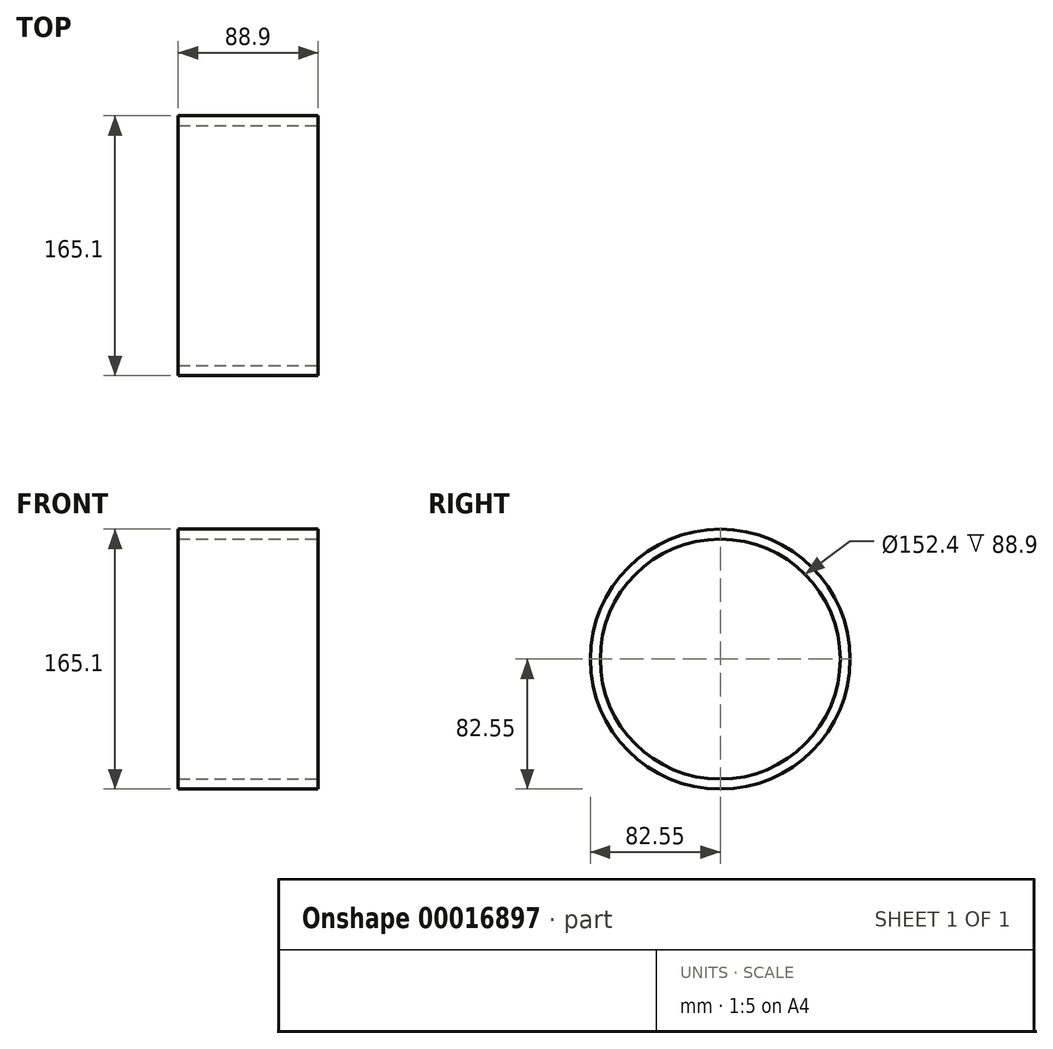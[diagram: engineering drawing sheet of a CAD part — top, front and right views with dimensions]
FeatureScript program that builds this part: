
annotation { "Feature Type Name" : "Feature", "Feature Type Description" : "" }
export const myFeature = defineFeature(function(context is Context, id is Id, definition is map)
    precondition{}
    {
        {
            var Q0;
            Q0=qCreatedBy(makeId("Right.planeOp"),FACE);
            var sketch = newSketch(context, id + "F0", { "sketchPlane" : qUnion([Q0])});
            skCircle(sketch, "E0", {"center": v(0, 0) * mm, "radius": 82.55 * mm});
            skSolve(sketch);
        }
        {
            var Q0;
            Q0=makeQuery(id+"F0.imprint","IMPRINT",FACE,{"disambiguationData":[TD([[makeQuery(id+"F0.imprint","IMPRINT",EDGE,{"derivedFrom":sQuery(id+"F0.wireOp",EDGE,"E0")}),1.0]])]});
            extrude(context, id + "F1", {"entities" : qUnion([Q0]), "depth" : 88.9 * mm});
        }
        {
            var Q0;
            Q0=makeQuery(id+"F1.opExtrude","CAP_FACE",FACE,{"disambiguationData":[OSD([sQuery(id+"F0.wireOp",EDGE,"E0")])],"isStart":false});
            var sketch = newSketch(context, id + "F2", { "sketchPlane" : qUnion([Q0])});
            skCircle(sketch, "E1", {"center": v(0, 0) * mm, "radius": 76.2 * mm});
            skSolve(sketch);
        }
        {
            var Q0;
            Q0=makeQuery(id+"F2.imprint","IMPRINT",FACE,{"disambiguationData":[TD([[makeQuery(id+"F2.imprint","IMPRINT",EDGE,{"derivedFrom":sQuery(id+"F2.wireOp",EDGE,"E1")}),1.0]])]});
            extrude(context, id + "F3", {"entities" : qUnion([Q0]), "operationType" : NewBodyOperationType.REMOVE, "oppositeDirection" : true, "depth" : 165.58 * mm});
        }
    });
